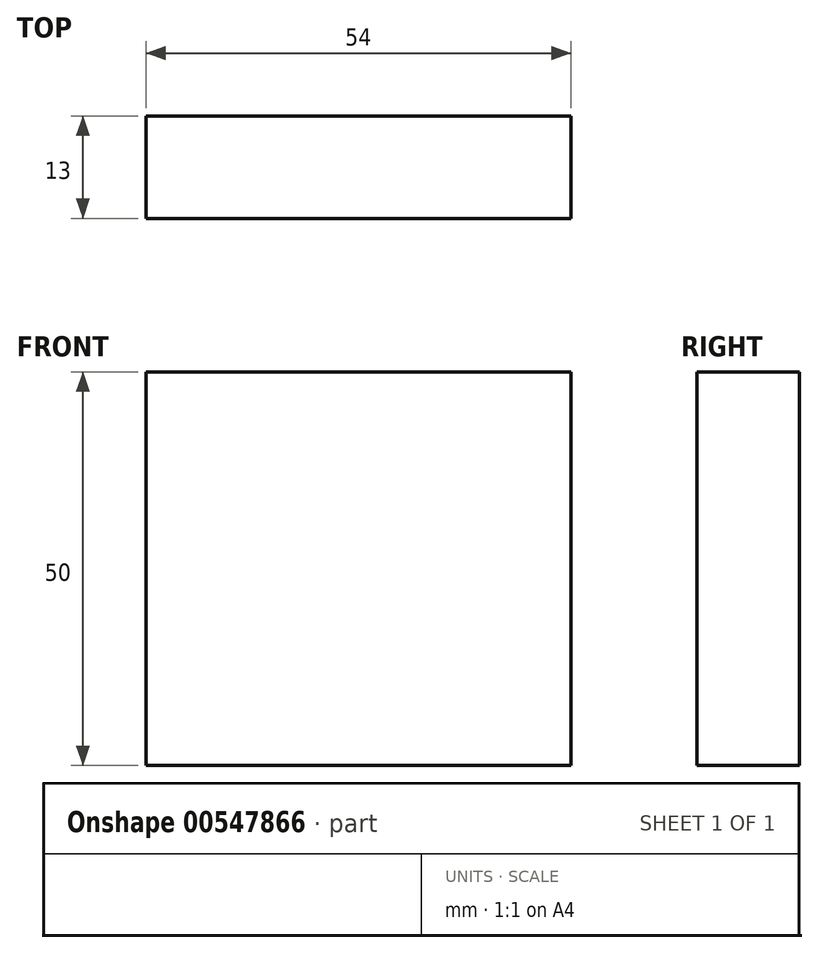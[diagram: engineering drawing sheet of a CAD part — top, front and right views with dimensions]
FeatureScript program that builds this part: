
annotation { "Feature Type Name" : "Feature", "Feature Type Description" : "" }
export const myFeature = defineFeature(function(context is Context, id is Id, definition is map)
    precondition{}
    {
        {
            var Q0;
            Q0=qCreatedBy(makeId("Front.planeOp"),FACE);
            var sketch = newSketch(context, id + "F0", { "sketchPlane" : qUnion([Q0])});
            skLineSegment(sketch, "E0.bottom", {"start": v(0, 0) * mm, "end": v(-54, 0) * mm});
            skLineSegment(sketch, "E0.top", {"start": v(0, 50) * mm, "end": v(-54, 50) * mm});
            skLineSegment(sketch, "E0.left", {"start": v(0, 0) * mm, "end": v(0, 50) * mm});
            skLineSegment(sketch, "E0.right", {"start": v(-54, 0) * mm, "end": v(-54, 50) * mm});
            skSolve(sketch);
        }
        {
            var Q0;
            Q0=makeQuery(id+"F0.imprint","IMPRINT",FACE,{"disambiguationData":[TD([[makeQuery(id+"F0.imprint","IMPRINT",EDGE,{"derivedFrom":sQuery(id+"F0.wireOp",EDGE,"E0.bottom")}),-1.0]])]});
            extrude(context, id + "F1", {"entities" : qUnion([Q0]), "depth" : 13 * mm, "offsetDistance" : 25 * mm});
        }
    });
